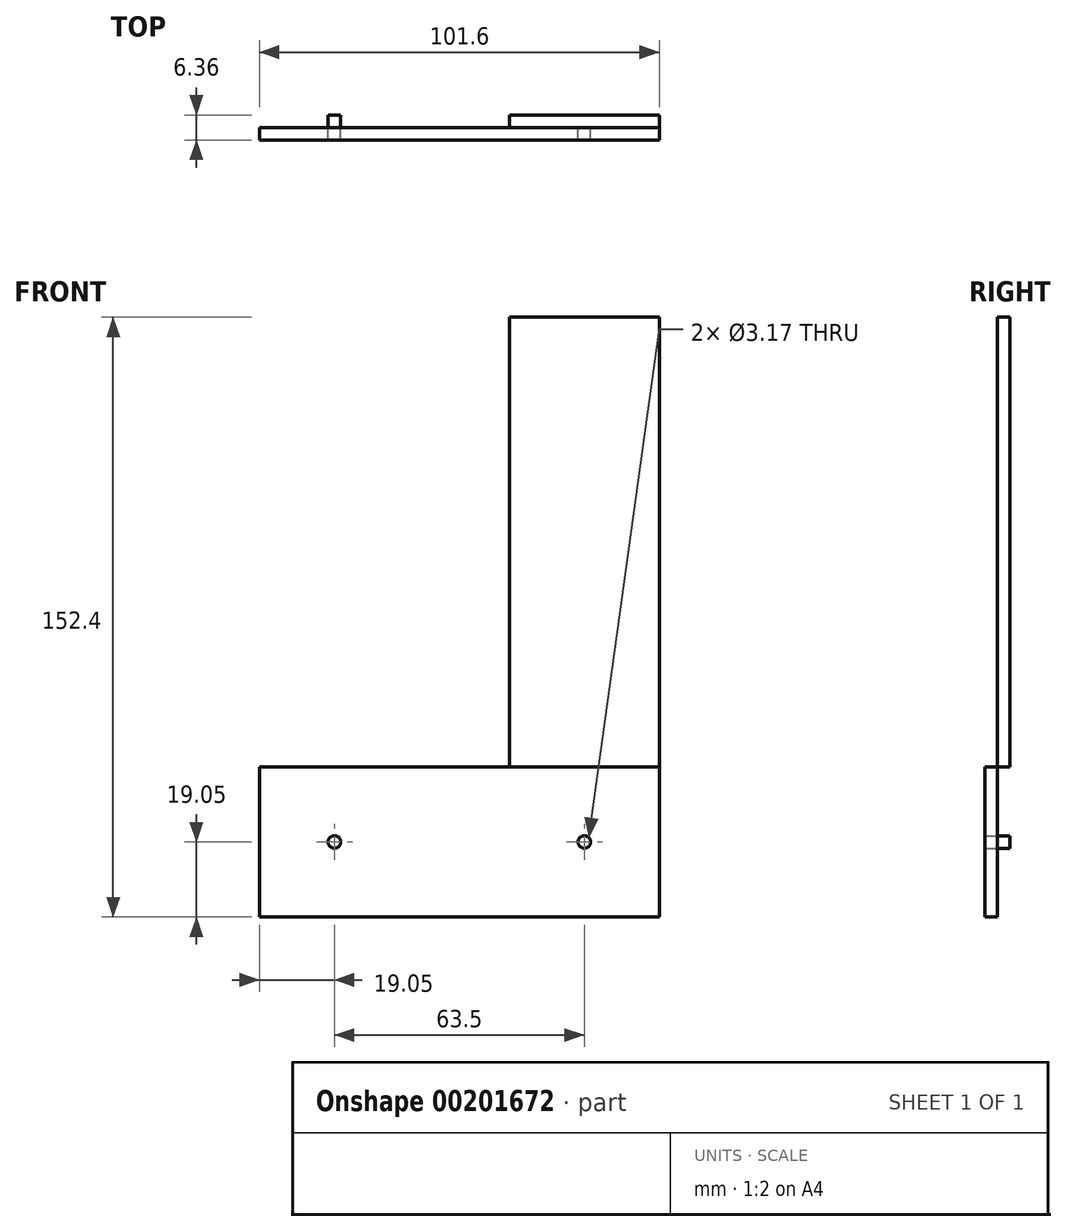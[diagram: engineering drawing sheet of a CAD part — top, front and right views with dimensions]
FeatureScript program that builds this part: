
annotation { "Feature Type Name" : "Feature", "Feature Type Description" : "" }
export const myFeature = defineFeature(function(context is Context, id is Id, definition is map)
    precondition{}
    {
        {
            var Q0;
            Q0=qCreatedBy(makeId("Front.planeOp"),FACE);
            var sketch = newSketch(context, id + "F0", { "sketchPlane" : qUnion([Q0])});
            skLineSegment(sketch, "E0.bottom", {"start": v(50.8, 19.05) * mm, "end": v(-50.8, 19.05) * mm});
            skLineSegment(sketch, "E0.top", {"start": v(50.8, -19.05) * mm, "end": v(-50.8, -19.05) * mm});
            skLineSegment(sketch, "E0.left", {"start": v(50.8, 19.05) * mm, "end": v(50.8, -19.05) * mm});
            skLineSegment(sketch, "E0.right", {"start": v(-50.8, 19.05) * mm, "end": v(-50.8, -19.05) * mm});
            skPoint(sketch, "E0.middle", {"position": v(0, 0) * mm});
            skLineSegment(sketch, "E1.bottom", {"start": v(50.8, -19.05) * mm, "end": v(12.7, -19.05) * mm});
            skLineSegment(sketch, "E1.top", {"start": v(50.8, 133.35) * mm, "end": v(12.7, 133.35) * mm});
            skLineSegment(sketch, "E1.left", {"start": v(50.8, -19.05) * mm, "end": v(50.8, 133.35) * mm});
            skLineSegment(sketch, "E1.right", {"start": v(12.7, -19.05) * mm, "end": v(12.7, 133.35) * mm});
            skCircle(sketch, "E2", {"center": v(31.75, 0) * mm, "radius": 1.59 * mm});
            skPoint(sketch, "E2.centerSnap0", {"position": v(31.75, 133.35) * mm});
            skCircle(sketch, "E3", {"center": v(-31.75, 0) * mm, "radius": 1.59 * mm});
            skSolve(sketch);
        }
        {
            var Q0;
            {var subQ1=sQuery(id+"F0.wireOp",EDGE,"E0.top");Q0=makeQuery(id+"F0.imprint","IMPRINT",FACE,{"disambiguationData":[TD([[makeQuery(id+"F0.imprint","IMPRINT",EDGE,{"derivedFrom":subQ1}),-1.0]])]});}
            var Q1;
            {var subQ1=sQuery(id+"F0.wireOp",EDGE,"E1.bottom");Q1=makeQuery(id+"F0.imprint","IMPRINT",FACE,{"disambiguationData":[TD([[makeQuery(id+"F0.imprint","IMPRINT",EDGE,{"derivedFrom":subQ1}),-1.0]])]});}
            extrude(context, id + "F1", {"entities" : qUnion([Q0, Q1]), "depth" : 3.17 * mm});
        }
        {
            var Q0;
            {var subQ5=sQuery(id+"F0.wireOp",EDGE,"E1.top");Q0=makeQuery(id+"F0.imprint","IMPRINT",FACE,{"disambiguationData":[TD([[makeQuery(id+"F0.imprint","IMPRINT",EDGE,{"derivedFrom":subQ5}),1.0]])]});}
            var Q1;
            {var subQ1=sQuery(id+"F0.wireOp",EDGE,"E1.bottom");Q1=makeQuery(id+"F0.imprint","IMPRINT",FACE,{"disambiguationData":[TD([[makeQuery(id+"F0.imprint","IMPRINT",EDGE,{"derivedFrom":subQ1}),-1.0]])]});}
            extrude(context, id + "F2", {"entities" : qUnion([Q0, Q1]), "oppositeDirection" : true, "depth" : 3.17 * mm});
        }
        {
            var Q0;
            Q0=makeQuery(id+"F0.imprint","IMPRINT",FACE,{"disambiguationData":[TD([[makeQuery(id+"F0.imprint","IMPRINT",EDGE,{"derivedFrom":sQuery(id+"F0.wireOp",EDGE,"E2")}),1.0]])]});
            var Q1;
            Q1=makeQuery(id+"F0.imprint","IMPRINT",FACE,{"disambiguationData":[TD([[makeQuery(id+"F0.imprint","IMPRINT",EDGE,{"derivedFrom":sQuery(id+"F0.wireOp",EDGE,"E3")}),1.0]])]});
            extrude(context, id + "F3", {"entities" : qUnion([Q0, Q1]), "endBound" : BoundingType.SYMMETRIC, "depth" : 6.35 * mm});
        }
    });
